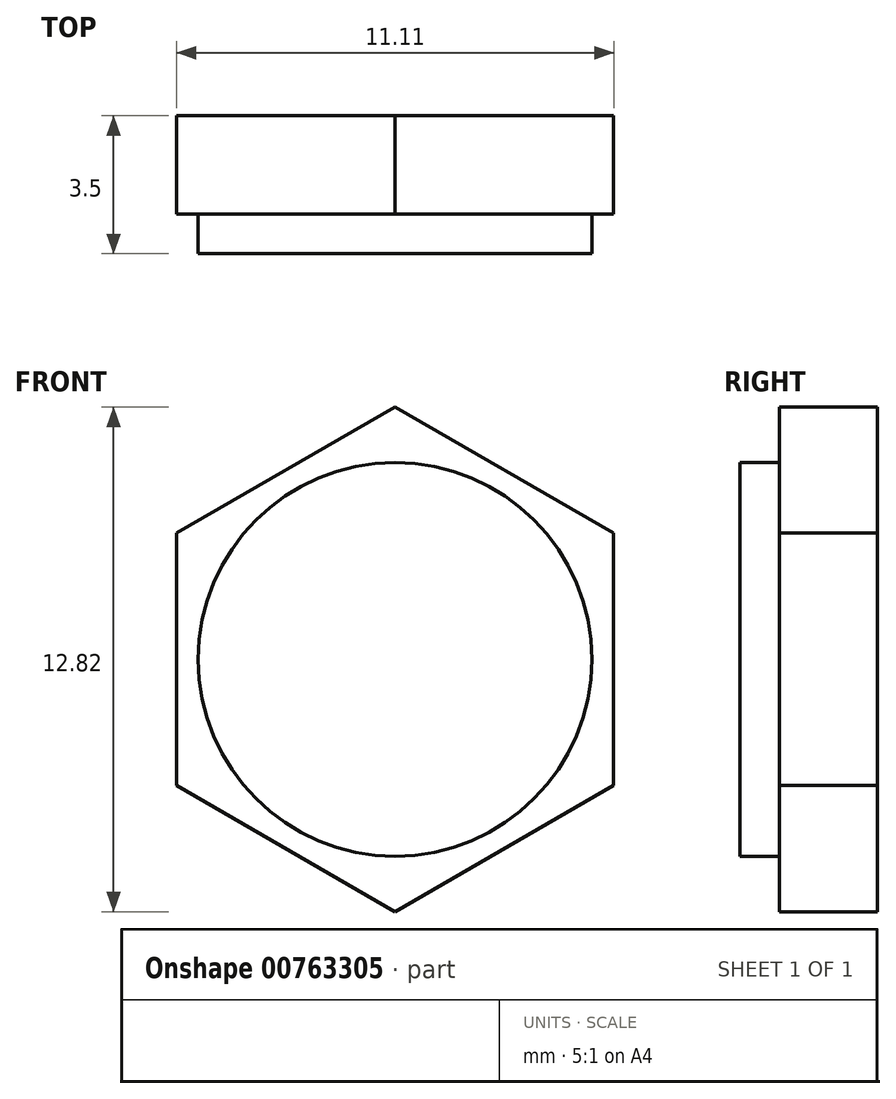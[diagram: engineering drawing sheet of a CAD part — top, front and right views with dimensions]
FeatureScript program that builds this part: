
annotation { "Feature Type Name" : "Feature", "Feature Type Description" : "" }
export const myFeature = defineFeature(function(context is Context, id is Id, definition is map)
    precondition{}
    {
        {
            var Q0;
            Q0=qCreatedBy(makeId("Front.planeOp"),FACE);
            var sketch = newSketch(context, id + "F0", { "sketchPlane" : qUnion([Q0])});
            skLineSegment(sketch, "E0.0", {"start": v(5.55, 3.2) * mm, "end": v(5.55, -3.2) * mm});
            skLineSegment(sketch, "E0.1", {"start": v(5.55, -3.2) * mm, "end": v(0, -6.41) * mm});
            skLineSegment(sketch, "E0.2", {"start": v(0, -6.41) * mm, "end": v(-5.55, -3.2) * mm});
            skLineSegment(sketch, "E0.3", {"start": v(-5.55, -3.2) * mm, "end": v(-5.55, 3.2) * mm});
            skLineSegment(sketch, "E0.4", {"start": v(-5.55, 3.2) * mm, "end": v(0, 6.41) * mm});
            skLineSegment(sketch, "E0.5", {"start": v(0, 6.41) * mm, "end": v(5.55, 3.2) * mm});
            skPoint(sketch, "E0.0.midPoint", {"position": v(5.55, 0) * mm});
            skPoint(sketch, "E0.cCircle.center.orphan", {"position": v(0, 0) * mm});
            skCircle(sketch, "E1", {"center": v(0, 0) * mm, "radius": 5 * mm});
            skSolve(sketch);
        }
        {
            var Q0;
            Q0=makeQuery(id+"F0.imprint","IMPRINT",FACE,{"disambiguationData":[TD([[makeQuery(id+"F0.imprint","IMPRINT",EDGE,{"derivedFrom":sQuery(id+"F0.wireOp",EDGE,"E1")}),1.0]])]});
            var Q1;
            Q1=makeQuery(id+"F0.imprint","IMPRINT",FACE,{"disambiguationData":[TD([[makeQuery(id+"F0.imprint","IMPRINT",EDGE,{"derivedFrom":sQuery(id+"F0.wireOp",EDGE,"E0.0")}),-1.0]])]});
            extrude(context, id + "F1", {"entities" : qUnion([Q0, Q1]), "depth" : 2.5 * mm, "offsetDistance" : 25 * mm});
        }
        {
            var Q0;
            Q0=makeQuery(id+"F0.imprint","IMPRINT",FACE,{"disambiguationData":[TD([[makeQuery(id+"F0.imprint","IMPRINT",EDGE,{"derivedFrom":sQuery(id+"F0.wireOp",EDGE,"E1")}),1.0]])]});
            extrude(context, id + "F2", {"entities" : qUnion([Q0]), "operationType" : NewBodyOperationType.ADD, "depth" : 3.5 * mm, "offsetDistance" : 25 * mm});
        }
    });
